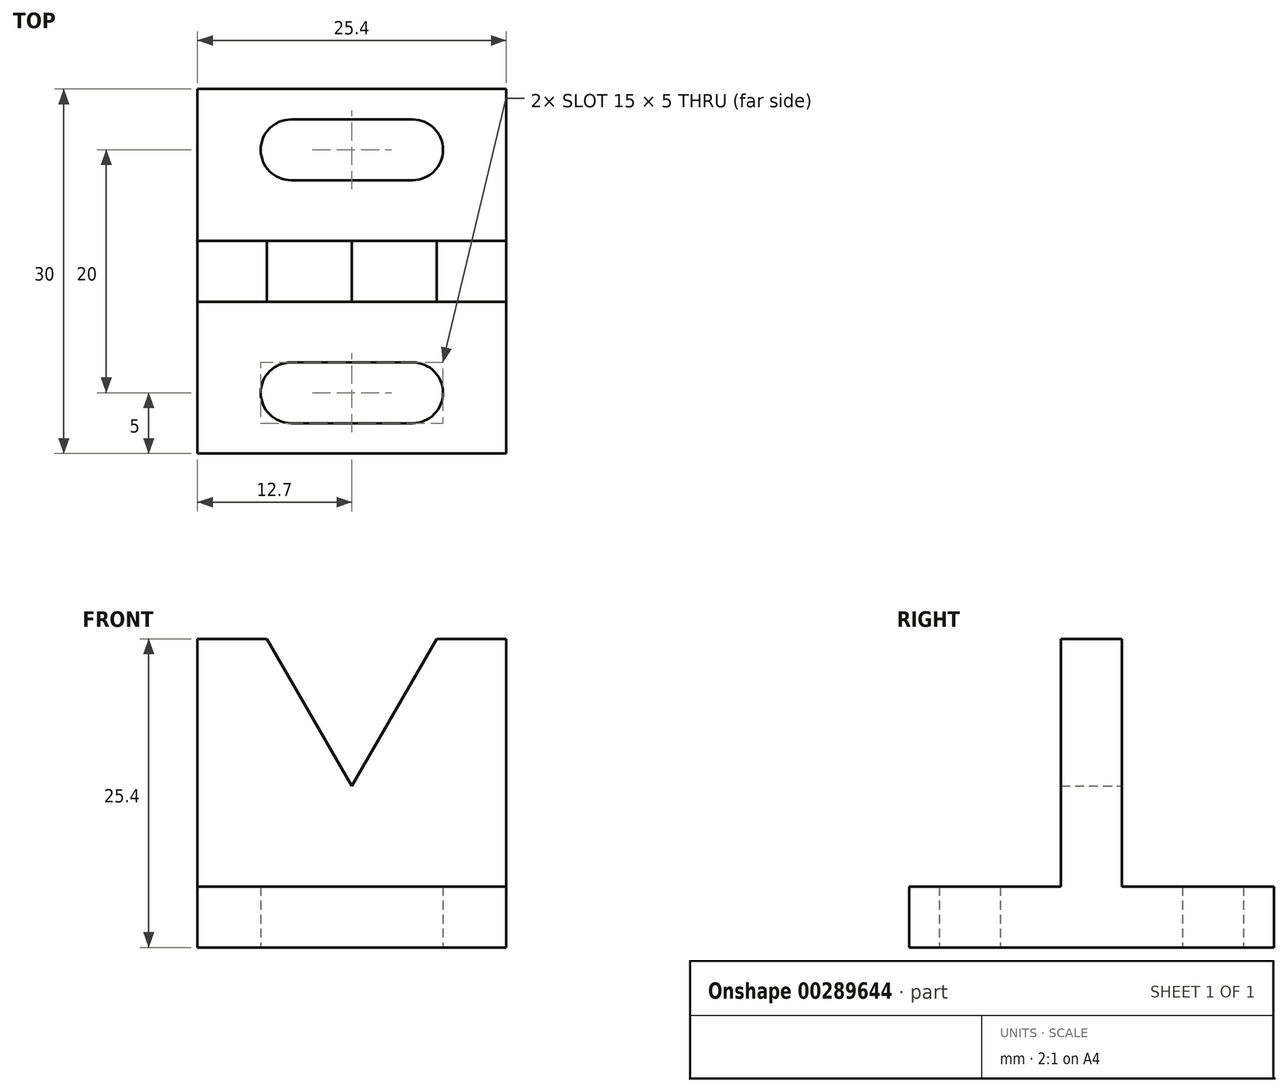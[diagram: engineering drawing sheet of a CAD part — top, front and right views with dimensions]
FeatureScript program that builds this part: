
annotation { "Feature Type Name" : "Feature", "Feature Type Description" : "" }
export const myFeature = defineFeature(function(context is Context, id is Id, definition is map)
    precondition{}
    {
        {
            var Q0;
            Q0=qCreatedBy(makeId("Front.planeOp"),FACE);
            var sketch = newSketch(context, id + "F0", { "sketchPlane" : qUnion([Q0])});
            skLineSegment(sketch, "E0", {"start": v(-12.7, -1.9) * mm, "end": v(-6.98, -1.9) * mm});
            skLineSegment(sketch, "E1", {"start": v(-6.98, -1.9) * mm, "end": v(0, -14) * mm});
            skLineSegment(sketch, "E2", {"start": v(0, -14) * mm, "end": v(6.99, -1.9) * mm});
            skLineSegment(sketch, "E3", {"start": v(6.99, -1.9) * mm, "end": v(12.7, -1.9) * mm});
            skLineSegment(sketch, "E4", {"start": v(12.7, -1.9) * mm, "end": v(12.7, -27.3) * mm});
            skLineSegment(sketch, "E5", {"start": v(12.7, -27.3) * mm, "end": v(-12.7, -27.3) * mm});
            skLineSegment(sketch, "E6", {"start": v(-12.7, -27.3) * mm, "end": v(-12.7, -1.9) * mm});
            skSolve(sketch);
        }
        {
            var Q0;
            Q0=makeQuery(id+"F0.imprint","IMPRINT",FACE,{"disambiguationData":[TD([[makeQuery(id+"F0.imprint","IMPRINT",EDGE,{"derivedFrom":sQuery(id+"F0.wireOp",EDGE,"E0")}),-1.0]])]});
            extrude(context, id + "F1", {"entities" : qUnion([Q0]), "endBound" : BoundingType.SYMMETRIC, "depth" : 5 * mm});
        }
        {
            var Q0;
            Q0=makeQuery(id+"F1.opExtrude","SWEPT_FACE",FACE,{"disambiguationData":[OSD([sQuery(id+"F0.wireOp",EDGE,"E5")])]});
            var sketch = newSketch(context, id + "F2", { "sketchPlane" : qUnion([Q0])});
            skLineSegment(sketch, "E7", {"start": v(-12.7, 2.5) * mm, "end": v(-12.7, 15) * mm});
            skLineSegment(sketch, "E8", {"start": v(-12.7, 15) * mm, "end": v(12.7, 15) * mm});
            skLineSegment(sketch, "E9", {"start": v(12.7, 15) * mm, "end": v(12.7, 2.5) * mm});
            skLineSegment(sketch, "E10", {"start": v(-5, 7.5) * mm, "end": v(5, 7.5) * mm});
            skArc(sketch, "E11", {"start": v(5, 7.5) * mm, "mid": v(7.5, 10) * mm, "end": v(5, 12.5) * mm});
            skLineSegment(sketch, "E12", {"start": v(5, 12.5) * mm, "end": v(-5, 12.5) * mm});
            skArc(sketch, "E13", {"start": v(-5, 12.5) * mm, "mid": v(-7.5, 10) * mm, "end": v(-5, 7.5) * mm});
            skLineSegment(sketch, "E14", {"start": v(-12.7, 10) * mm, "end": v(12.7, 10) * mm, "construction": true});
            skLineSegment(sketch, "E15.MirrorCS", {"start": v(-12.7, -15) * mm, "end": v(12.7, -15) * mm});
            skLineSegment(sketch, "E16.MirrorCS", {"start": v(12.7, -15) * mm, "end": v(12.7, -2.5) * mm});
            skArc(sketch, "E17.MirrorCS", {"start": v(5, -7.5) * mm, "mid": v(7.5, -10) * mm, "end": v(5, -12.5) * mm});
            skLineSegment(sketch, "E18.MirrorCS", {"start": v(-12.7, -10) * mm, "end": v(12.7, -10) * mm, "construction": true});
            skLineSegment(sketch, "E19.MirrorCS", {"start": v(5, -12.5) * mm, "end": v(-5, -12.5) * mm});
            skLineSegment(sketch, "E20.MirrorCS", {"start": v(-5, -7.5) * mm, "end": v(5, -7.5) * mm});
            skArc(sketch, "E21.MirrorCS", {"start": v(-5, -12.5) * mm, "mid": v(-7.5, -10) * mm, "end": v(-5, -7.5) * mm});
            skLineSegment(sketch, "E22.MirrorCS", {"start": v(-12.7, -2.5) * mm, "end": v(-12.7, -15) * mm});
            skSolve(sketch);
        }
        {
            var Q0;
            Q0=makeQuery(id+"F2.imprint","IMPRINT",FACE,{"disambiguationData":[TD([[makeQuery(id+"F2.imprint","IMPRINT",EDGE,{"derivedFrom":sQuery(id+"F2.wireOp",EDGE,"E7")}),-1.0]])]});
            var Q1;
            Q1=makeQuery(id+"F2.imprint","IMPRINT",FACE,{"disambiguationData":[TD([[makeQuery(id+"F2.imprint","IMPRINT",EDGE,{"derivedFrom":sQuery(id+"F2.wireOp",EDGE,"E15.MirrorCS")}),1.0]])]});
            extrude(context, id + "F3", {"entities" : qUnion([Q0, Q1]), "operationType" : NewBodyOperationType.ADD, "oppositeDirection" : true, "depth" : 5 * mm});
        }
    });
